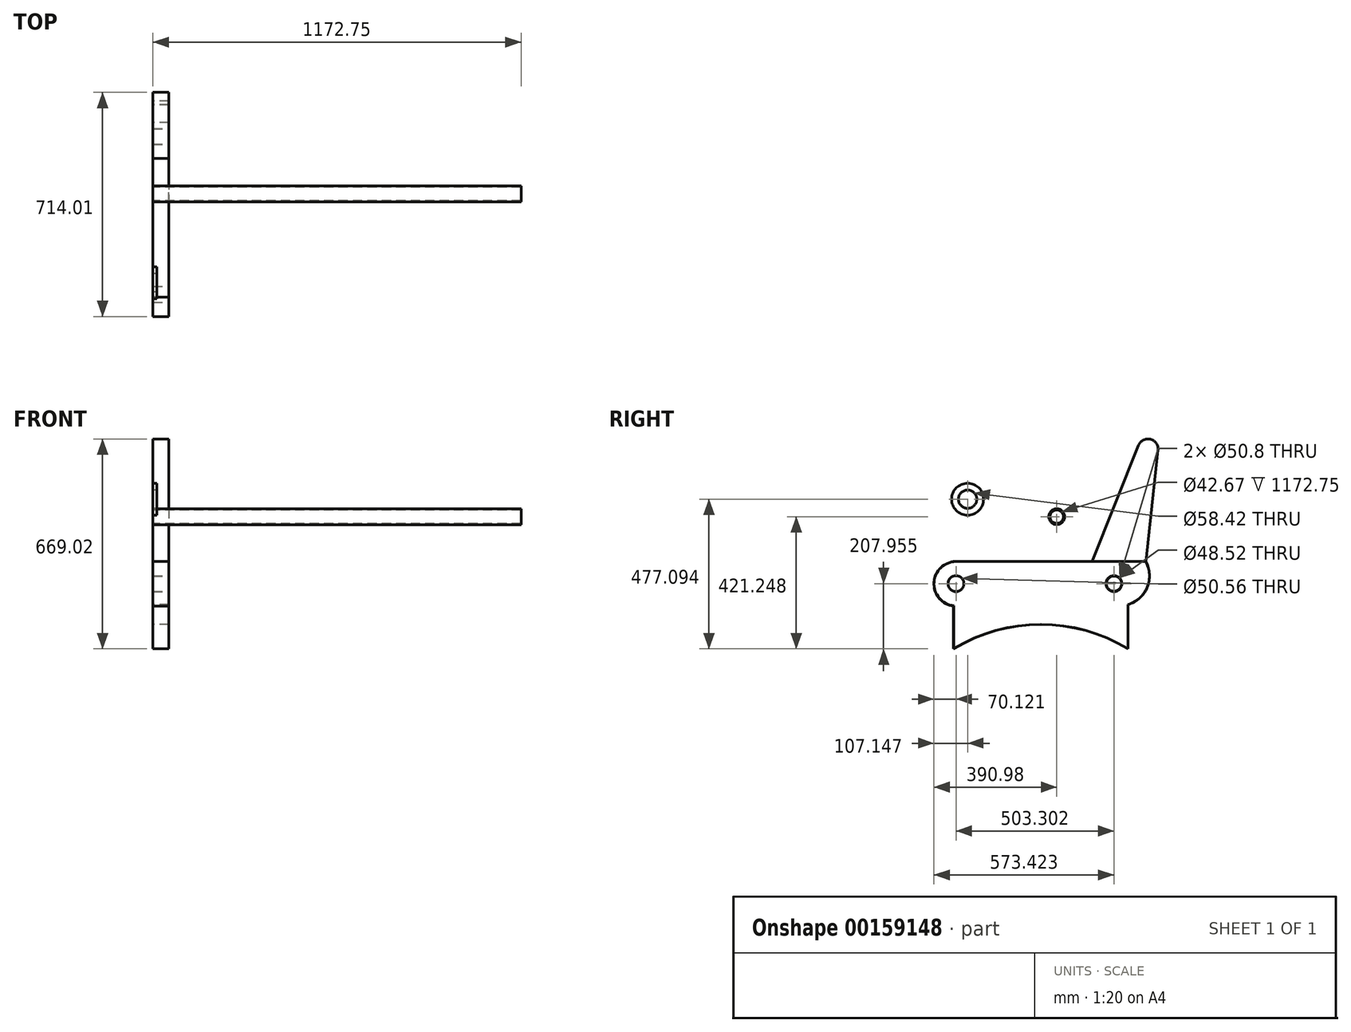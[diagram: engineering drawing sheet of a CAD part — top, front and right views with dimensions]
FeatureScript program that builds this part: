
annotation { "Feature Type Name" : "Feature", "Feature Type Description" : "" }
export const myFeature = defineFeature(function(context is Context, id is Id, definition is map)
    precondition{}
    {
        {
            var Q0;
            Q0=qCreatedBy(makeId("Right.planeOp"),FACE);
            var sketch = newSketch(context, id + "F0", { "sketchPlane" : qUnion([Q0])});
            skLineSegment(sketch, "E0", {"start": v(0, 0) * mm, "end": v(-320.86, 0) * mm});
            skArc(sketch, "E1", {"start": v(-320.86, 0) * mm, "mid": v(-390.98, -70.12) * mm, "end": v(-320.86, -140.25) * mm});
            skLineSegment(sketch, "E2", {"start": v(-320.86, -140.25) * mm, "end": v(208.7, -140.25) * mm});
            skArc(sketch, "E3", {"start": v(208.7, -140.25) * mm, "mid": v(283.75, -90.2) * mm, "end": v(284.67, 0) * mm});
            skLineSegment(sketch, "E4", {"start": v(284.67, 0) * mm, "end": v(322.85, 355.13) * mm});
            skArc(sketch, "E5", {"start": v(322.85, 355.13) * mm, "mid": v(298.46, 390) * mm, "end": v(260.61, 370.55) * mm});
            skLineSegment(sketch, "E6", {"start": v(260.61, 370.55) * mm, "end": v(113.17, 0) * mm});
            skLineSegment(sketch, "E7", {"start": v(113.17, 0) * mm, "end": v(0, 0) * mm});
            skSolve(sketch);
        }
        {
            var Q0;
            Q0=makeQuery(id+"F0.imprint","IMPRINT",FACE,{"disambiguationData":[TD([[makeQuery(id+"F0.imprint","IMPRINT",EDGE,{"derivedFrom":sQuery(id+"F0.wireOp",EDGE,"E0")}),1.0]])]});
            extrude(context, id + "F1", {"entities" : qUnion([Q0]), "depth" : 50.8 * mm});
        }
        {
            var Q0;
            Q0=qCreatedBy(makeId("Right.planeOp"),FACE);
            var sketch = newSketch(context, id + "F2", { "sketchPlane" : qUnion([Q0])});
            skLineSegment(sketch, "E8", {"start": v(-327.77, -142.13) * mm, "end": v(-327.77, -278) * mm});
            skArc(sketch, "E9", {"start": v(227.16, -278) * mm, "mid": v(-50.3, -199.83) * mm, "end": v(-327.77, -278) * mm});
            skLineSegment(sketch, "E10", {"start": v(227.16, -278) * mm, "end": v(227.16, -121) * mm});
            skLineSegment(sketch, "E11", {"start": v(227.16, -121) * mm, "end": v(-327.77, -121) * mm});
            skLineSegment(sketch, "E12", {"start": v(-327.77, -121) * mm, "end": v(-327.77, -142.13) * mm});
            skSolve(sketch);
        }
        {
            var Q0;
            Q0 = qSketchRegion(id + "F2", true);
            extrude(context, id + "F3", {"entities" : qUnion([Q0]), "operationType" : NewBodyOperationType.ADD, "depth" : 50.8 * mm});
        }
        {
            var Q0;
            Q0=makeQuery(id+"F3.boolean.opBoolean","MERGE",FACE,{"derivedFrom":[makeQuery(id+"F1.opExtrude","CAP_FACE",FACE,{"disambiguationData":[OSD([sQuery(id+"F0.wireOp",EDGE,"E0"),sQuery(id+"F0.wireOp",EDGE,"E1"),sQuery(id+"F0.wireOp",EDGE,"E2"),sQuery(id+"F0.wireOp",EDGE,"E3"),sQuery(id+"F0.wireOp",EDGE,"E4"),sQuery(id+"F0.wireOp",EDGE,"E5"),sQuery(id+"F0.wireOp",EDGE,"E6"),sQuery(id+"F0.wireOp",EDGE,"E7")])],"isStart":false}),makeQuery(id+"F3.opExtrude","CAP_FACE",FACE,{"disambiguationData":[OSD([sQuery(id+"F2.wireOp",EDGE,"E8"),sQuery(id+"F2.wireOp",EDGE,"E9"),sQuery(id+"F2.wireOp",EDGE,"E10"),sQuery(id+"F2.wireOp",EDGE,"E11"),sQuery(id+"F2.wireOp",EDGE,"E12")])],"isStart":false})]});
            var sketch = newSketch(context, id + "F4", { "sketchPlane" : qUnion([Q0])});
            skCircle(sketch, "E13", {"center": v(-320.86, -70.12) * mm, "radius": 25.4 * mm});
            skCircle(sketch, "E14", {"center": v(182.44, -70.12) * mm, "radius": 25.4 * mm});
            skSolve(sketch);
        }
        {
            var Q0;
            Q0 = qSketchRegion(id + "F4", true);
            extrude(context, id + "F5", {"entities" : qUnion([Q0]), "operationType" : NewBodyOperationType.REMOVE, "endBound" : BoundingType.THROUGH_ALL, "oppositeDirection" : true, "depth" : 25.4 * mm});
        }
        {
            var Q0;
            Q0=qCreatedBy(makeId("Right.planeOp"),FACE);
            var sketch = newSketch(context, id + "F6", { "sketchPlane" : qUnion([Q0])});
            skCircle(sketch, "E15", {"center": v(-283.83, 199.01) * mm, "radius": 29.21 * mm});
            skCircle(sketch, "E16", {"center": v(-283.83, 199.01) * mm, "radius": 50.8 * mm});
            skSolve(sketch);
        }
        {
            var Q0;
            Q0 = qSketchRegion(id + "F6", true);
            extrude(context, id + "F7", {"entities" : qUnion([Q0]), "depth" : 12.7 * mm});
        }
        {
            var Q0;
            Q0=qCreatedBy(makeId("Right.planeOp"),FACE);
            var sketch = newSketch(context, id + "F8", { "sketchPlane" : qUnion([Q0])});
            skCircle(sketch, "E17", {"center": v(0, 143.17) * mm, "radius": 21.34 * mm});
            skCircle(sketch, "E18", {"center": v(0, 143.17) * mm, "radius": 25.15 * mm});
            skSolve(sketch);
        }
        {
            var Q0;
            Q0 = qSketchRegion(id + "F8", true);
            var Q1;
            Q1=makeQuery(id+"F8.imprint","IMPRINT",FACE,{"disambiguationData":[TD([[makeQuery(id+"F8.imprint","IMPRINT",EDGE,{"derivedFrom":sQuery(id+"F8.wireOp",EDGE,"E17")}),-1.0]])]});
            extrude(context, id + "F9", {"entities" : qUnion([Q0, Q1]), "depth" : 1172.75 * mm});
        }
        {
            var Q0;
            Q0=qCreatedBy(makeId("Right.planeOp"),FACE);
            var sketch = newSketch(context, id + "F10", { "sketchPlane" : qUnion([Q0])});
            skLineSegment(sketch, "E19", {"start": v(0, 0) * mm, "end": v(282.74, 0) * mm});
            skArc(sketch, "E20", {"start": v(227.2, -136.53) * mm, "mid": v(288.65, -81.96) * mm, "end": v(282.74, 0) * mm});
            skLineSegment(sketch, "E21", {"start": v(227.2, -136.53) * mm, "end": v(227.2, -278.08) * mm});
            skArc(sketch, "E22", {"start": v(227.2, -278.08) * mm, "mid": v(-50.83, -199.88) * mm, "end": v(-328.86, -278.08) * mm});
            skLineSegment(sketch, "E23", {"start": v(-328.86, -278.08) * mm, "end": v(-328.86, -142.1) * mm});
            skArc(sketch, "E24", {"start": v(-328.86, 0) * mm, "mid": v(-390.97, -71.05) * mm, "end": v(-328.86, -142.1) * mm});
            skLineSegment(sketch, "E25", {"start": v(-328.86, 0) * mm, "end": v(0, 0) * mm});
            skSolve(sketch);
        }
        {
            var Q0;
            Q0 = qSketchRegion(id + "F10", true);
            extrude(context, id + "F11", {"entities" : qUnion([Q0]), "depth" : 50.8 * mm});
        }
        {
            var Q0;
            Q0=makeQuery(id+"F3.boolean.opBoolean","MERGE",FACE,{"derivedFrom":[makeQuery(id+"F1.opExtrude","CAP_FACE",FACE,{"disambiguationData":[OSD([sQuery(id+"F0.wireOp",EDGE,"E0"),sQuery(id+"F0.wireOp",EDGE,"E1"),sQuery(id+"F0.wireOp",EDGE,"E2"),sQuery(id+"F0.wireOp",EDGE,"E3"),sQuery(id+"F0.wireOp",EDGE,"E4"),sQuery(id+"F0.wireOp",EDGE,"E5"),sQuery(id+"F0.wireOp",EDGE,"E6"),sQuery(id+"F0.wireOp",EDGE,"E7")])],"isStart":false}),makeQuery(id+"F3.opExtrude","CAP_FACE",FACE,{"disambiguationData":[OSD([sQuery(id+"F2.wireOp",EDGE,"E8"),sQuery(id+"F2.wireOp",EDGE,"E9"),sQuery(id+"F2.wireOp",EDGE,"E10"),sQuery(id+"F2.wireOp",EDGE,"E11"),sQuery(id+"F2.wireOp",EDGE,"E12")])],"isStart":false})]});
            var sketch = newSketch(context, id + "F12", { "sketchPlane" : qUnion([Q0])});
            skCircle(sketch, "E26", {"center": v(-320.86, -70.12) * mm, "radius": 25.28 * mm});
            skCircle(sketch, "E27", {"center": v(182.44, -70.12) * mm, "radius": 24.26 * mm});
            skSolve(sketch);
        }
        {
            var Q0;
            Q0 = qSketchRegion(id + "F12", true);
            extrude(context, id + "F13", {"entities" : qUnion([Q0]), "operationType" : NewBodyOperationType.REMOVE, "endBound" : BoundingType.THROUGH_ALL, "oppositeDirection" : true, "depth" : 25.4 * mm});
        }
    });
